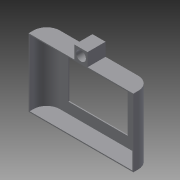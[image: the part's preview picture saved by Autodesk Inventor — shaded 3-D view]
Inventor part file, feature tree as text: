
AUTODESK INVENTOR PART (.ipt)
format: ipt  version: 2015 SP1 (Build 190203100, 203)  size: 131,072 bytes
history: native  units: in
note: dims shown in document units (in); Inventor stores cm internally (conversion verified against a paired STEP export)
features: sketch x3, extrude x2, fillet x2, projected_geometry x2, shell x1, hole x1
ambient origin geometry x8: Origin, YZ Plane, XZ Plane, XY Plane, X Axis, Y Axis, Z Axis, Center Point
bodies: Solid1 (feature_tree)
feature tree (11):
  extrude  "Extrusion1"  Depth=2.2677in
  shell  "Shell1"  Thickness=2.7008in
  fillet  "Fillet1"  Radius=2.1024in
  extrude  "Extrusion2"  Depth=0.6875in TaperAngle=0.0deg
  hole  "Hole1"  [1 undecoded]
  fillet  "Fillet2"  Radius=0.0394in
  sketch  "Sketch1"  dims[d0=1.7008in d1=2.2677in d2=2.7008in d3=2.1024in]
  sketch  "Sketch2"  dims[d4=0.25in d5=0.6875in d6=0.0in]
  projected_geometry  "Projected Loop1"
  sketch  "Sketch3"  dims[d7=4.0in d8=2.6024in d9=0.0394in d10=0.5in d11=0.5in d13=0.5in d14=0.0in d15=0.375in d16=0.75in d17=0.375in d18=0.25in d19=0.5635in d20=1.0in d21=0.8108in d22=0.5in]
  projected_geometry  "Projected Loop2"
note: 1 required parameter value undecoded (feature->parameter linkage not recoverable at this tier; creation-order binding heuristic only, values carry confidence <= 0.55)
